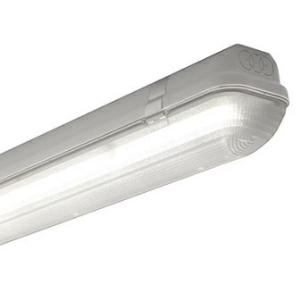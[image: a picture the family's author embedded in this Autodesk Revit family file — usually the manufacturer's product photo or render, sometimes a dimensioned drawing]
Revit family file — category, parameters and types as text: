
# Revit family: 3f_filippi_-_3f_linda_hq_3f_filippi_-_58871_-_3f_linda_led_1x30w-940_l1570
name_source: partatom
category: Lighting Fixtures
units: mm (PartAtom-declared; Revit-internal decimal feet)

## family parameters
Cut with Voids When Loaded = No
Host = Face
Light Source = No
Part Type = Normal
Room Calculation Point = No
Round Connector Dimension = Use Diameter
Shared = No

## types (1)
- 3F Filippi - 3F Linda HQ (1 x LED, 4015 lm, 33.5 W, 4000 K)
    Apparent Load = 34 VA
    Approval mark = CE
    CIE Flux Codes = 44 77 94 97 100
    Color Rendering = 90
    Color Temperature = 4000 K
    Control Gear = Electronic ballast
    Default Elevation = 1800 mm
    Description = ILLUMINOTECHNICAL
Luminous efficiency 100% (DLOR 97%, ULOR 3%).
Initial luminous flux of the luminaire 4015 lm.
Controlled symmetric distribution.
Installation Interdistance Transv.D = 1.77 x hu - Long.D = 1.17 x hu.
Tabular UGR (CIE 117 - 4H-8H; S=0.25H; 70/50/20): RUG 21.2 - 22.2.
Beam angle: 109° - 64°.
Luminous efficacy 120 lm/W.
Lifetime (L93/B10): 30000 h. (tq+25°C)
Lifetime (L90/B10): 50000 h. (tq+25°C)
Lifetime (L85/B10): 80000 h. (tq+25°C)
Lifetime (L80/B10): 100000 h. (tq+25°C)
Lifetime (L85/B10): 50000 h. (tq+35°C)
Sudden decreased luminous flux after 50000 hours: 0% (C0).
Photobiological safety in compliance with IEC/TR 62778: RG0 risk exempt, (IEC 62471).
In compliance with IEC/EN 62722-2-1 - IEC/EN 62717 standards.

SOURCE
Linear LED module 30W/940.
Energy efficiency class (UE 2019/2020 - UE 2019/2015): E.
CIE 13.3 Colour rendering index: CRI >90 (R9 >50%).
IES TM-30 Fidelity Index: Rf = 92 Rg = 101.
CCT nominal colour temperature 4000 K.
Colour initial tolerance (MacAdam): SDCM 3.

MECHANICAL
Self-extinguishing V2 polycarbonate housing, injection moulded, RAL 7035 grey.
Ecologic anti-aging injected sealing gasket.
Diffuser in self-extinguishing V2 polycarbonate, photo-engraved interior, UV stabilised, injection moulded with smooth outer surface, tamper-proof opening.
Gear-holder reflector in hot-dip galvanised steel, painted with white polyester base.
Snug fit safety snap-lock clips for diffuser mounting in stainless steel, screwdriver opening.
Fixing brackets in stainless steel.
Possibility for technicians to access the interior of the luminaire.
Luminaire with limited surface temperature. - D - (EN 60598-2-24)
Dimensions: 1570x100 mm, height 100 mm. Weight 2.447 kg.
IP66 protection degree.
Mechanical strength to impacts IK10 (20 joule).
Glow-wire test resistance 850°C.

ELECTRICAL
Halogen Free electronic wiring 230V-50/60Hz, power factor 0.90, THD <25%, constant output current, SELV, class I, 1 driver.
Power of the luminaire 33.5 W.
ENEC - CE.
SAFE FLICKER: PstLM=<1 and SVM=<0.4 (IEC TR 61547-1 and IEC TR 63158), to ensure a more comfortable and safe light.
Luminaire compliant with EN 60598-2-22 for power supply from a centralised emergency system CPSS (Central Power Supply System), not incorporated in the luminaire - high risk areas excluded. The default power and flux are 100% in AC and 100% in DC.
Ambient temperature from -20°C to +35°C.
Temperature class T6 max 85°C.
Relative humidity UR: <85%.

INSTALLATION
Ceiling / Suspended / Wall.
All accessories dedicated to this product are available on the Catalog and on our website www.3F-Filippi.com.

APPLICATIONS
Suitable product for food production plants (HACCP), IFS (Food Version 6), BRC (GSFS Food Version 7).
Dry, dusty indoor environments, subject to occasional water splashes.
Virtually shatterproof polycarbonate compatibly with the fumes / atmospheres that compromise the elasticity of plastic materials.
Not suitable for installation on surfaces subject to important vibrations, exposed to weather conditions, on ropes or poles.
Suitable for illumination of public car parks and parking grounds referred to DIN 67528:2018-04.

WARNING
Fixture not suitable for cold stores with an ambient temperature <0°C and/or relative humidity >85%.
Luminaire designed for disposal/recycling at end-of-life.
Replaceable (LED only) light source by a professional. Replaceable control gear by a professional.
    Height = 100 mm  [stored 0.328084 ft]
    Lamp = 1 x LED
    Lamp Light Flux = 4015 lm
    Lamp Power = 33.5 W
    Lamp count = 1
    Length = 1570 mm
    Lifetime = 50000 h
    Luminous efficacy = 120 lm/W
    Manufacturer = 3F Filippi
    ModVariant = No
    Model = 3F Filippi - 58871 - 3F Linda LED 1x30W-940 L1570
    Mounting Place = Ceiling
    Mounting Type = Pendant
    Number of Poles = 1
    OnlyDefault = Yes
    Power Factor = 1
    Product Name = 3F Filippi - 3F Linda HQ
    Product group = pendant luminaire
    ProductGroupID = 9
    Protection Class = Protection class I
    Protection Degree = IP 66
    RLX_Detail_Level = 1
    RLX_Emergency_Light_Flux = 0 lm
    RLX_Emergency_Type = 0
    RLX_Emergency_Type_DB = No
    RlxData = <blob elided: 69029 chars, md5=1309dab9>
    Socket = socket
    Standby Power = 0 W
    System Light Flux = 4015 lm
    System Power = 34 W
    Type Comments = Product without accessories
    Type Image = 3ffilippi_3f_linda_led_1x.jpg
    URL = http://relux.com
    VarID = ---
    Voltage = 0 V
    Weight = 0.00 kg
    Width = 100 mm  [stored 0.328084 ft]

note: [stored X ft] marks values corroborated as IEEE doubles in the binary element streams (Revit-internal decimal feet)

## geometry (parser evidence)
native form markers: Blend x4, Sweep x8
no freeform markers — native parametric forms only
